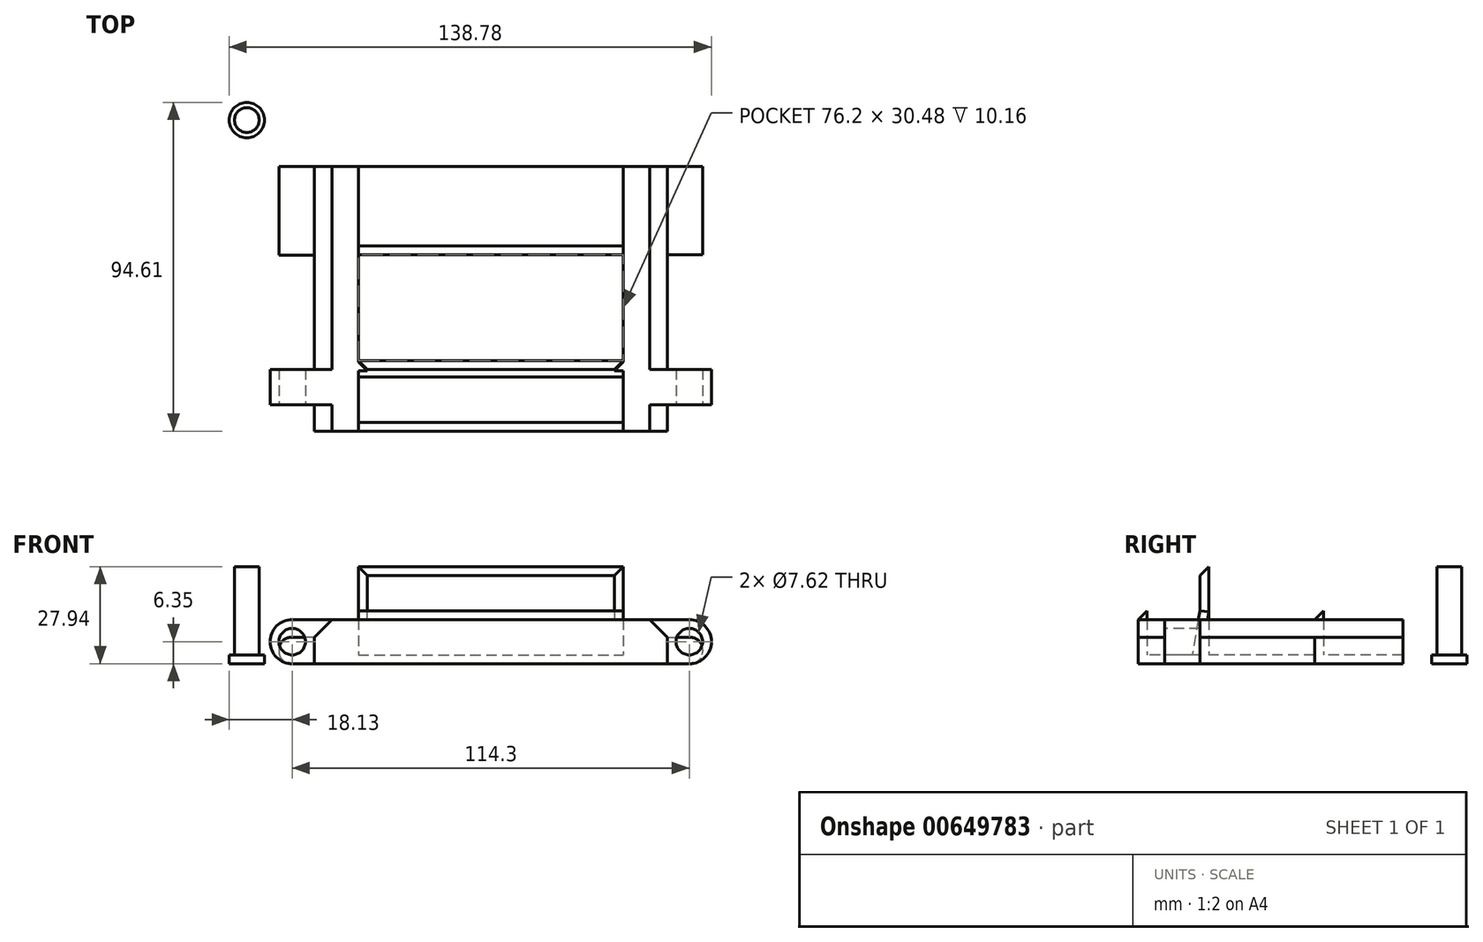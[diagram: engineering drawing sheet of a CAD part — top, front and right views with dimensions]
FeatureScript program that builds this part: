
annotation { "Feature Type Name" : "Feature", "Feature Type Description" : "" }
export const myFeature = defineFeature(function(context is Context, id is Id, definition is map)
    precondition{}
    {
        {
            var Q0;
            Q0=qCreatedBy(makeId("Top.planeOp"),FACE);
            var sketch = newSketch(context, id + "F0", { "sketchPlane" : qUnion([Q0])});
            skLineSegment(sketch, "E0.bottom", {"start": v(-50.8, 38.1) * mm, "end": v(50.8, 38.1) * mm});
            skLineSegment(sketch, "E0.top", {"start": v(-50.8, -38.1) * mm, "end": v(50.8, -38.1) * mm});
            skLineSegment(sketch, "E0.left", {"start": v(-50.8, 38.1) * mm, "end": v(-50.8, -38.1) * mm});
            skLineSegment(sketch, "E0.right", {"start": v(50.8, 38.1) * mm, "end": v(50.8, -38.1) * mm});
            skPoint(sketch, "E0.middle", {"position": v(0, 0) * mm});
            skSolve(sketch);
        }
        {
            var Q0;
            Q0 = qSketchRegion(id + "F0", true);
            extrude(context, id + "F1", {"entities" : qUnion([Q0]), "depth" : 2.54 * mm, "offsetDistance" : 25.4 * mm});
        }
        {
            var Q0;
            Q0=qCreatedBy(makeId("Top.planeOp"),FACE);
            var sketch = newSketch(context, id + "F2", { "sketchPlane" : qUnion([Q0])});
            skLineSegment(sketch, "E1.bottom", {"start": v(-50.8, 38.1) * mm, "end": v(50.8, 38.1) * mm});
            skLineSegment(sketch, "E1.top", {"start": v(-50.8, -38.1) * mm, "end": v(50.8, -38.1) * mm});
            skLineSegment(sketch, "E1.left", {"start": v(-50.8, 38.1) * mm, "end": v(-50.8, -38.1) * mm});
            skLineSegment(sketch, "E1.right", {"start": v(50.8, 38.1) * mm, "end": v(50.8, -38.1) * mm});
            skPoint(sketch, "E1.middle", {"position": v(0, 0) * mm});
            skLineSegment(sketch, "E2", {"start": v(-63.5, -30.48) * mm, "end": v(-63.5, -20.32) * mm});
            skLineSegment(sketch, "E3", {"start": v(-63.5, -20.32) * mm, "end": v(-50.8, -20.32) * mm});
            skLineSegment(sketch, "E4", {"start": v(-63.5, -30.48) * mm, "end": v(-50.8, -30.48) * mm});
            skLineSegment(sketch, "E5", {"start": v(0, 8.2) * mm, "end": v(0, -13.6) * mm});
            skLineSegment(sketch, "E6.MirrorCS", {"start": v(63.5, -20.32) * mm, "end": v(50.8, -20.32) * mm});
            skLineSegment(sketch, "E7.MirrorCS", {"start": v(63.5, -30.48) * mm, "end": v(63.5, -20.32) * mm});
            skLineSegment(sketch, "E8.MirrorCS", {"start": v(63.5, -30.48) * mm, "end": v(50.8, -30.48) * mm});
            skSolve(sketch);
        }
        {
            var Q0;
            Q0=makeQuery(id+"F2.imprint","IMPRINT",FACE,{"disambiguationData":[TD([[makeQuery(id+"F2.imprint","IMPRINT",EDGE,{"derivedFrom":sQuery(id+"F2.wireOp",EDGE,"E2")}),-1.0]])]});
            var Q1;
            {var subQ0=sQuery(id+"F2.wireOp",EDGE,"E6.MirrorCS");Q1=makeQuery(id+"F2.imprint","IMPRINT",FACE,{"disambiguationData":[TD([[makeQuery(id+"F2.imprint","IMPRINT",EDGE,{"derivedFrom":subQ0}),1.0]])]});}
            extrude(context, id + "F3", {"entities" : qUnion([Q0, Q1]), "operationType" : NewBodyOperationType.ADD, "depth" : 12.7 * mm, "offsetDistance" : 25.4 * mm});
        }
        {
            var Q0;
            Q0=makeQuery(id+"F3.opExtrude","CAP_EDGE",EDGE,{"disambiguationData":[OSD([sQuery(id+"F2.wireOp",EDGE,"E2")])],"isStart":false});
            var Q1;
            Q1=makeQuery(id+"F3.opExtrude","CAP_EDGE",EDGE,{"disambiguationData":[OSD([sQuery(id+"F2.wireOp",EDGE,"E2")])],"isStart":true});
            var Q2;
            Q2=makeQuery(id+"F3.opExtrude","CAP_EDGE",EDGE,{"disambiguationData":[OSD([sQuery(id+"F2.wireOp",EDGE,"E7.MirrorCS")])],"isStart":false});
            var Q3;
            Q3=makeQuery(id+"F3.opExtrude","CAP_EDGE",EDGE,{"disambiguationData":[OSD([sQuery(id+"F2.wireOp",EDGE,"E7.MirrorCS")])],"isStart":true});
            fillet(context, id + "F4", {"entities" : qUnion([Q0, Q1, Q2, Q3]), "radius" : 6.35 * mm, "tangentPropagation" : true, "allowEdgeOverflow" : false});
        }
        {
            var Q0;
            Q0=makeQuery(id+"F3.opExtrude","SWEPT_FACE",FACE,{"disambiguationData":[OSD([sQuery(id+"F2.wireOp",EDGE,"E4")])]});
            var sketch = newSketch(context, id + "F5", { "sketchPlane" : qUnion([Q0])});
            skCircle(sketch, "E9", {"center": v(-57.15, 6.35) * mm, "radius": 3.81 * mm});
            skLineSegment(sketch, "E10", {"start": v(0, 11.47) * mm, "end": v(0, 19.86) * mm});
            skCircle(sketch, "E11.MirrorC", {"center": v(57.15, 6.35) * mm, "radius": 3.81 * mm});
            skSolve(sketch);
        }
        {
            var Q0;
            Q0 = qSketchRegion(id + "F5", true);
            extrude(context, id + "F6", {"entities" : qUnion([Q0]), "operationType" : NewBodyOperationType.REMOVE, "oppositeDirection" : true, "depth" : 25.4 * mm, "offsetDistance" : 25.4 * mm});
        }
        {
            var Q0;
            Q0=makeQuery(id+"F1.opExtrude","CAP_FACE",FACE,{"disambiguationData":[OSD([sQuery(id+"F0.wireOp",EDGE,"E0.bottom"),sQuery(id+"F0.wireOp",EDGE,"E0.top"),sQuery(id+"F0.wireOp",EDGE,"E0.left"),sQuery(id+"F0.wireOp",EDGE,"E0.right")])],"isStart":false});
            var sketch = newSketch(context, id + "F7", { "sketchPlane" : qUnion([Q0])});
            skLineSegment(sketch, "E12.bottom", {"start": v(-50.8, 38.1) * mm, "end": v(-38.1, 38.1) * mm});
            skLineSegment(sketch, "E12.top", {"start": v(-50.8, -38.1) * mm, "end": v(-38.1, -38.1) * mm});
            skLineSegment(sketch, "E12.left", {"start": v(-50.8, 38.1) * mm, "end": v(-50.8, -38.1) * mm});
            skLineSegment(sketch, "E12.right", {"start": v(-38.1, 38.1) * mm, "end": v(-38.1, -38.1) * mm});
            skLineSegment(sketch, "E13.bottom", {"start": v(50.8, 38.1) * mm, "end": v(38.1, 38.1) * mm});
            skLineSegment(sketch, "E13.top", {"start": v(50.8, -38.1) * mm, "end": v(38.1, -38.1) * mm});
            skLineSegment(sketch, "E13.left", {"start": v(50.8, 38.1) * mm, "end": v(50.8, -38.1) * mm});
            skLineSegment(sketch, "E13.right", {"start": v(38.1, 38.1) * mm, "end": v(38.1, -38.1) * mm});
            skSolve(sketch);
        }
        {
            var Q0;
            Q0 = qSketchRegion(id + "F7", true);
            extrude(context, id + "F8", {"entities" : qUnion([Q0]), "operationType" : NewBodyOperationType.ADD, "depth" : 10.16 * mm, "offsetDistance" : 25.4 * mm});
        }
        {
            var Q0;
            {var subQ2=sQuery(id+"F7.wireOp",EDGE,"E12.left");Q0=makeQuery(id+"F8.boolean.opBoolean","SPLIT",EDGE,{"disambiguationData":[TD([makeQuery(id+"F1.opExtrude","SWEPT_FACE",FACE,{"disambiguationData":[OSD([sQuery(id+"F0.wireOp",EDGE,"E0.bottom")])]})])],"derivedFrom":makeQuery(id+"F8.opExtrude","CAP_EDGE",EDGE,{"disambiguationData":[OSD([subQ2])],"isStart":false})});}
            var Q1;
            {var subQ1=sQuery(id+"F7.wireOp",EDGE,"E12.left");Q1=makeQuery(id+"F8.boolean.opBoolean","SPLIT",EDGE,{"disambiguationData":[TD([makeQuery(id+"F1.opExtrude","SWEPT_FACE",FACE,{"disambiguationData":[OSD([sQuery(id+"F0.wireOp",EDGE,"E0.top")])]})])],"derivedFrom":makeQuery(id+"F8.opExtrude","CAP_EDGE",EDGE,{"disambiguationData":[OSD([subQ1])],"isStart":false})});}
            var Q2;
            {var subQ2=sQuery(id+"F7.wireOp",EDGE,"E13.left");Q2=makeQuery(id+"F8.boolean.opBoolean","SPLIT",EDGE,{"disambiguationData":[TD([makeQuery(id+"F1.opExtrude","SWEPT_FACE",FACE,{"disambiguationData":[OSD([sQuery(id+"F0.wireOp",EDGE,"E0.bottom")])]})])],"derivedFrom":makeQuery(id+"F8.opExtrude","CAP_EDGE",EDGE,{"disambiguationData":[OSD([subQ2])],"isStart":false})});}
            var Q3;
            {var subQ1=sQuery(id+"F7.wireOp",EDGE,"E13.left");Q3=makeQuery(id+"F8.boolean.opBoolean","SPLIT",EDGE,{"disambiguationData":[TD([makeQuery(id+"F1.opExtrude","SWEPT_FACE",FACE,{"disambiguationData":[OSD([sQuery(id+"F0.wireOp",EDGE,"E0.top")])]})])],"derivedFrom":makeQuery(id+"F8.opExtrude","CAP_EDGE",EDGE,{"disambiguationData":[OSD([subQ1])],"isStart":false})});}
            chamfer(context, id + "F9", {"entities" : qUnion([Q0, Q1, Q2, Q3]), "width" : 5.08 * mm, "tangentPropagation" : true});
        }
        {
            var Q0;
            Q0=makeQuery(id+"F1.opExtrude","CAP_FACE",FACE,{"disambiguationData":[OSD([sQuery(id+"F0.wireOp",EDGE,"E0.bottom"),sQuery(id+"F0.wireOp",EDGE,"E0.top"),sQuery(id+"F0.wireOp",EDGE,"E0.left"),sQuery(id+"F0.wireOp",EDGE,"E0.right")])],"isStart":false});
            var sketch = newSketch(context, id + "F10", { "sketchPlane" : qUnion([Q0])});
            skLineSegment(sketch, "E14.bottom", {"start": v(-38.1, -38.1) * mm, "end": v(38.1, -38.1) * mm});
            skLineSegment(sketch, "E14.top", {"start": v(-38.1, -35.56) * mm, "end": v(38.1, -35.56) * mm});
            skLineSegment(sketch, "E14.left", {"start": v(-38.1, -38.1) * mm, "end": v(-38.1, -35.56) * mm});
            skLineSegment(sketch, "E14.right", {"start": v(38.1, -38.1) * mm, "end": v(38.1, -35.56) * mm});
            skLineSegment(sketch, "E15", {"start": v(-38.1, -35.56) * mm, "end": v(-38.1, -20.32) * mm});
            skLineSegment(sketch, "E16.bottom", {"start": v(-38.1, -20.32) * mm, "end": v(38.1, -20.32) * mm});
            skLineSegment(sketch, "E16.top", {"start": v(-38.1, -17.78) * mm, "end": v(38.1, -17.78) * mm});
            skLineSegment(sketch, "E16.left", {"start": v(-38.1, -20.32) * mm, "end": v(-38.1, -17.78) * mm});
            skLineSegment(sketch, "E16.right", {"start": v(38.1, -20.32) * mm, "end": v(38.1, -17.78) * mm});
            skLineSegment(sketch, "E17", {"start": v(-38.1, -17.78) * mm, "end": v(-38.1, 12.7) * mm});
            skLineSegment(sketch, "E18.bottom", {"start": v(-38.1, 12.7) * mm, "end": v(38.1, 12.7) * mm});
            skLineSegment(sketch, "E18.top", {"start": v(-38.1, 15.24) * mm, "end": v(38.1, 15.24) * mm});
            skLineSegment(sketch, "E18.left", {"start": v(-38.1, 12.7) * mm, "end": v(-38.1, 15.24) * mm});
            skLineSegment(sketch, "E18.right", {"start": v(38.1, 12.7) * mm, "end": v(38.1, 15.24) * mm});
            skSolve(sketch);
        }
        {
            var Q0;
            Q0 = qSketchRegion(id + "F10", true);
            extrude(context, id + "F11", {"entities" : qUnion([Q0]), "operationType" : NewBodyOperationType.ADD, "depth" : 12.7 * mm, "offsetDistance" : 25.4 * mm});
        }
        {
            var Q0;
            Q0=makeQuery(id+"F11.opExtrude","CAP_FACE",FACE,{"disambiguationData":[OSD([sQuery(id+"F10.wireOp",EDGE,"E16.bottom"),sQuery(id+"F10.wireOp",EDGE,"E16.top"),sQuery(id+"F10.wireOp",EDGE,"E16.left"),sQuery(id+"F10.wireOp",EDGE,"E16.right")])],"isStart":false});
            extrude(context, id + "F12", {"entities" : qUnion([Q0]), "operationType" : NewBodyOperationType.ADD, "depth" : 12.7 * mm, "offsetDistance" : 25.4 * mm});
        }
        {
            var Q0;
            {var subQ0=sQuery(id+"F10.wireOp",EDGE,"E16.bottom");Q0=makeQuery(id+"F12.boolean.opBoolean","MERGE",FACE,{"derivedFrom":[makeQuery(id+"F11.opExtrude","SWEPT_FACE",FACE,{"disambiguationData":[OSD([subQ0])]}),makeQuery(id+"F12.opExtrude","SWEPT_FACE",FACE,{"disambiguationData":[OSD([subQ0])]})]});}
            var sketch = newSketch(context, id + "F13", { "sketchPlane" : qUnion([Q0])});
            skLineSegment(sketch, "E19.bottom", {"start": v(-38.1, 2.54) * mm, "end": v(38.1, 2.54) * mm});
            skLineSegment(sketch, "E19.top", {"start": v(-38.1, 27.94) * mm, "end": v(38.1, 27.94) * mm});
            skLineSegment(sketch, "E19.left", {"start": v(-38.1, 2.54) * mm, "end": v(-38.1, 27.94) * mm});
            skLineSegment(sketch, "E19.right", {"start": v(38.1, 2.54) * mm, "end": v(38.1, 27.94) * mm});
            skLineSegment(sketch, "E20.bottom", {"start": v(-38.1, 15.24) * mm, "end": v(38.1, 15.24) * mm});
            skLineSegment(sketch, "E20.left", {"start": v(-38.1, 15.24) * mm, "end": v(-38.1, 2.54) * mm});
            skLineSegment(sketch, "E20.right", {"start": v(38.1, 15.24) * mm, "end": v(38.1, 2.54) * mm});
            skSolve(sketch);
        }
        {
            var Q0;
            {var subQ3=sQuery(id+"F13.wireOp",EDGE,"E20.bottom");Q0=makeQuery(id+"F13.imprint","IMPRINT",FACE,{"disambiguationData":[TD([[makeQuery(id+"F13.imprint","IMPRINT",EDGE,{"derivedFrom":subQ3}),-1.0]])]});}
            extrude(context, id + "F14", {"entities" : qUnion([Q0]), "operationType" : NewBodyOperationType.ADD, "depth" : 2.54 * mm, "offsetDistance" : 25.4 * mm});
        }
        {
            var Q0;
            Q0=makeQuery(id+"F14.opExtrude","CAP_EDGE",EDGE,{"disambiguationData":[OSD([sQuery(id+"F13.wireOp",EDGE,"E20.bottom")])],"isStart":false});
            chamfer(context, id + "F15", {"entities" : qUnion([Q0]), "chamferType" : ChamferType.OFFSET_ANGLE, "width" : 2.54 * mm, "oppositeDirection" : false, "angle" : 80 * degree, "tangentPropagation" : true});
        }
        {
            var Q0;
            Q0=makeQuery(id+"F12.opExtrude","CAP_EDGE",EDGE,{"disambiguationData":[OSD([sQuery(id+"F10.wireOp",EDGE,"E16.bottom")])],"isStart":false});
            var Q1;
            Q1=makeQuery(id+"F11.opExtrude","CAP_EDGE",EDGE,{"disambiguationData":[OSD([sQuery(id+"F10.wireOp",EDGE,"E14.bottom")])],"isStart":false});
            var Q2;
            Q2=makeQuery(id+"F11.opExtrude","CAP_EDGE",EDGE,{"disambiguationData":[OSD([sQuery(id+"F10.wireOp",EDGE,"E18.bottom")])],"isStart":false});
            chamfer(context, id + "F16", {"entities" : qUnion([Q0, Q1, Q2]), "width" : 2.54 * mm, "tangentPropagation" : true});
        }
        {
            var Q0;
            {var subQ0=sQuery(id+"F10.wireOp",EDGE,"E16.left");var subQ1=sQuery(id+"F10.wireOp",EDGE,"E16.bottom");var subQ2=sQuery(id+"F10.wireOp",EDGE,"E15");Q0=makeQuery(id+"F12.boolean.opBoolean","MERGE",EDGE,{"derivedFrom":[makeQuery(id+"F11.boolean.opBoolean","SPLIT",EDGE,{"disambiguationData":[topologyDisambiguationEdgeConnected([makeQuery(id+"F11.opExtrude","SWEPT_FACE",FACE,{"disambiguationData":[OSD([subQ0])]})])],"derivedFrom":makeQuery(id+"F11.opExtrude","SWEPT_EDGE",EDGE,{"disambiguationData":[OSD([subQ2,subQ1,subQ0])]})}),makeQuery(id+"F12.opExtrude","SWEPT_EDGE",EDGE,{"disambiguationData":[OSD([subQ2,subQ1,subQ0])]})]});}
            var Q1;
            {var subQ0=sQuery(id+"F10.wireOp",EDGE,"E16.left");Q1=makeQuery(id+"F15.opChamfer","BLEND_EDGE",EDGE,{"blendedFrom":[makeQuery(id+"F14.opExtrude","CAP_EDGE",EDGE,{"disambiguationData":[OSD([sQuery(id+"F13.wireOp",EDGE,"E20.bottom")])],"isStart":false}),makeQuery(id+"F14.boolean.opBoolean","MERGE",FACE,{"derivedFrom":[makeQuery(id+"F12.boolean.opBoolean","MERGE",FACE,{"derivedFrom":[makeQuery(id+"F11.opExtrude","SWEPT_FACE",FACE,{"disambiguationData":[OSD([subQ0])]}),makeQuery(id+"F12.opExtrude","SWEPT_FACE",FACE,{"disambiguationData":[OSD([subQ0])]})]}),makeQuery(id+"F14.opExtrude","SWEPT_FACE",FACE,{"disambiguationData":[OSD([sQuery(id+"F13.wireOp",EDGE,"E20.left")])]})]})],"blendedInto":[makeQuery(id+"F14.boolean.opBoolean","MERGE",FACE,{"derivedFrom":[makeQuery(id+"F12.boolean.opBoolean","MERGE",FACE,{"derivedFrom":[makeQuery(id+"F11.opExtrude","SWEPT_FACE",FACE,{"disambiguationData":[OSD([subQ0])]}),makeQuery(id+"F12.opExtrude","SWEPT_FACE",FACE,{"disambiguationData":[OSD([subQ0])]})]}),makeQuery(id+"F14.opExtrude","SWEPT_FACE",FACE,{"disambiguationData":[OSD([sQuery(id+"F13.wireOp",EDGE,"E20.left")])]})]})]});}
            var Q2;
            {var subQ0=sQuery(id+"F10.wireOp",EDGE,"E16.right");var subQ1=sQuery(id+"F10.wireOp",EDGE,"E16.bottom");var subQ2=sQuery(id+"F7.wireOp",EDGE,"E13.right");Q2=makeQuery(id+"F12.boolean.opBoolean","MERGE",EDGE,{"derivedFrom":[makeQuery(id+"F11.boolean.opBoolean","SPLIT",EDGE,{"disambiguationData":[topologyDisambiguationEdgeConnected([makeQuery(id+"F11.opExtrude","SWEPT_FACE",FACE,{"disambiguationData":[OSD([subQ0])]})])],"derivedFrom":makeQuery(id+"F11.opExtrude","SWEPT_EDGE",EDGE,{"disambiguationData":[OSD([subQ2,subQ1,subQ0])]})}),makeQuery(id+"F12.opExtrude","SWEPT_EDGE",EDGE,{"disambiguationData":[OSD([subQ2,subQ1,subQ0])]})]});}
            var Q3;
            {var subQ0=sQuery(id+"F10.wireOp",EDGE,"E16.right");Q3=makeQuery(id+"F15.opChamfer","BLEND_EDGE",EDGE,{"blendedFrom":[makeQuery(id+"F14.opExtrude","CAP_EDGE",EDGE,{"disambiguationData":[OSD([sQuery(id+"F13.wireOp",EDGE,"E20.bottom")])],"isStart":false}),makeQuery(id+"F14.boolean.opBoolean","MERGE",FACE,{"derivedFrom":[makeQuery(id+"F12.boolean.opBoolean","MERGE",FACE,{"derivedFrom":[makeQuery(id+"F11.opExtrude","SWEPT_FACE",FACE,{"disambiguationData":[OSD([subQ0])]}),makeQuery(id+"F12.opExtrude","SWEPT_FACE",FACE,{"disambiguationData":[OSD([subQ0])]})]}),makeQuery(id+"F14.opExtrude","SWEPT_FACE",FACE,{"disambiguationData":[OSD([sQuery(id+"F13.wireOp",EDGE,"E20.right")])]})]})],"blendedInto":[makeQuery(id+"F14.boolean.opBoolean","MERGE",FACE,{"derivedFrom":[makeQuery(id+"F12.boolean.opBoolean","MERGE",FACE,{"derivedFrom":[makeQuery(id+"F11.opExtrude","SWEPT_FACE",FACE,{"disambiguationData":[OSD([subQ0])]}),makeQuery(id+"F12.opExtrude","SWEPT_FACE",FACE,{"disambiguationData":[OSD([subQ0])]})]}),makeQuery(id+"F14.opExtrude","SWEPT_FACE",FACE,{"disambiguationData":[OSD([sQuery(id+"F13.wireOp",EDGE,"E20.right")])]})]})]});}
            chamfer(context, id + "F17", {"entities" : qUnion([Q0, Q1, Q2, Q3]), "width" : 2.54 * mm, "tangentPropagation" : true});
        }
        {
            var Q0;
            Q0=qCreatedBy(makeId("Top.planeOp"),FACE);
            var sketch = newSketch(context, id + "F18", { "sketchPlane" : qUnion([Q0])});
            skCircle(sketch, "E21", {"center": v(-70.2, 51.43) * mm, "radius": 5.08 * mm});
            skSolve(sketch);
        }
        {
            var Q0;
            Q0 = qSketchRegion(id + "F18", true);
            extrude(context, id + "F19", {"entities" : qUnion([Q0]), "depth" : 2.54 * mm, "offsetDistance" : 25.4 * mm});
        }
        {
            var Q0;
            Q0=makeQuery(id+"F19.opExtrude","CAP_FACE",FACE,{"disambiguationData":[OSD([sQuery(id+"F18.wireOp",EDGE,"E21")])],"isStart":false});
            var sketch = newSketch(context, id + "F20", { "sketchPlane" : qUnion([Q0])});
            skCircle(sketch, "E22", {"center": v(-70.2, 51.43) * mm, "radius": 3.56 * mm});
            skSolve(sketch);
        }
        {
            var Q0;
            Q0 = qSketchRegion(id + "F20", true);
            extrude(context, id + "F21", {"entities" : qUnion([Q0]), "operationType" : NewBodyOperationType.ADD, "depth" : 25.4 * mm, "offsetDistance" : 25.4 * mm});
        }
        {
            var Q0;
            Q0=qCreatedBy(makeId("Top.planeOp"),FACE);
            var sketch = newSketch(context, id + "F22", { "sketchPlane" : qUnion([Q0])});
            skLineSegment(sketch, "E23.bottom", {"start": v(50.8, 38.1) * mm, "end": v(-50.8, 38.1) * mm});
            skLineSegment(sketch, "E23.top", {"start": v(50.8, -38.1) * mm, "end": v(-50.8, -38.1) * mm});
            skLineSegment(sketch, "E23.left", {"start": v(50.8, 38.1) * mm, "end": v(50.8, -38.1) * mm});
            skLineSegment(sketch, "E23.right", {"start": v(-50.8, 38.1) * mm, "end": v(-50.8, -38.1) * mm});
            skPoint(sketch, "E23.middle", {"position": v(0, 0) * mm});
            skLineSegment(sketch, "E24", {"start": v(-50.8, 38.1) * mm, "end": v(-50.8, 12.7) * mm});
            skLineSegment(sketch, "E25", {"start": v(50.8, 38.1) * mm, "end": v(50.8, 12.7) * mm});
            skLineSegment(sketch, "E26.bottom", {"start": v(-50.8, 38.1) * mm, "end": v(-60.96, 38.1) * mm});
            skLineSegment(sketch, "E26.top", {"start": v(-50.8, 12.55) * mm, "end": v(-60.96, 12.55) * mm});
            skLineSegment(sketch, "E26.left", {"start": v(-50.8, 38.1) * mm, "end": v(-50.8, 12.55) * mm});
            skLineSegment(sketch, "E26.right", {"start": v(-60.96, 38.1) * mm, "end": v(-60.96, 12.55) * mm});
            skLineSegment(sketch, "E27.bottom", {"start": v(50.8, 38.1) * mm, "end": v(60.96, 38.1) * mm});
            skLineSegment(sketch, "E27.top", {"start": v(50.8, 12.7) * mm, "end": v(60.96, 12.7) * mm});
            skLineSegment(sketch, "E27.right", {"start": v(60.96, 38.1) * mm, "end": v(60.96, 12.7) * mm});
            skSolve(sketch);
        }
        {
            var Q0;
            {var subQ3=sQuery(id+"F22.wireOp",EDGE,"E26.bottom");Q0=makeQuery(id+"F22.imprint","IMPRINT",FACE,{"disambiguationData":[TD([[makeQuery(id+"F22.imprint","IMPRINT",EDGE,{"derivedFrom":subQ3}),1.0]])]});}
            var Q1;
            Q1=makeQuery(id+"F22.imprint","IMPRINT",FACE,{"disambiguationData":[TD([[makeQuery(id+"F22.imprint","IMPRINT",EDGE,{"derivedFrom":sQuery(id+"F22.wireOp",EDGE,"E27.bottom")}),-1.0]])]});
            extrude(context, id + "F23", {"entities" : qUnion([Q0, Q1]), "operationType" : NewBodyOperationType.ADD, "depth" : 7.62 * mm, "offsetDistance" : 25.4 * mm});
        }
        {
            var Q0;
            Q0=makeQuery(id+"F23.opExtrude","CAP_EDGE",EDGE,{"disambiguationData":[OSD([sQuery(id+"F22.wireOp",EDGE,"E26.right")])],"isStart":false});
            var Q1;
            Q1=makeQuery(id+"F23.opExtrude","CAP_EDGE",EDGE,{"disambiguationData":[OSD([sQuery(id+"F22.wireOp",EDGE,"E26.right")])],"isStart":true});
            var Q2;
            Q2=makeQuery(id+"F23.opExtrude","CAP_EDGE",EDGE,{"disambiguationData":[OSD([sQuery(id+"F22.wireOp",EDGE,"E27.right")])],"isStart":false});
            var Q3;
            Q3=makeQuery(id+"F23.opExtrude","CAP_EDGE",EDGE,{"disambiguationData":[OSD([sQuery(id+"F22.wireOp",EDGE,"E27.right")])],"isStart":true});
            fillet(context, id + "F24", {"entities" : qUnion([Q0, Q1, Q2, Q3]), "radius" : 3.56 * mm, "tangentPropagation" : true, "allowEdgeOverflow" : false});
        }
    });
